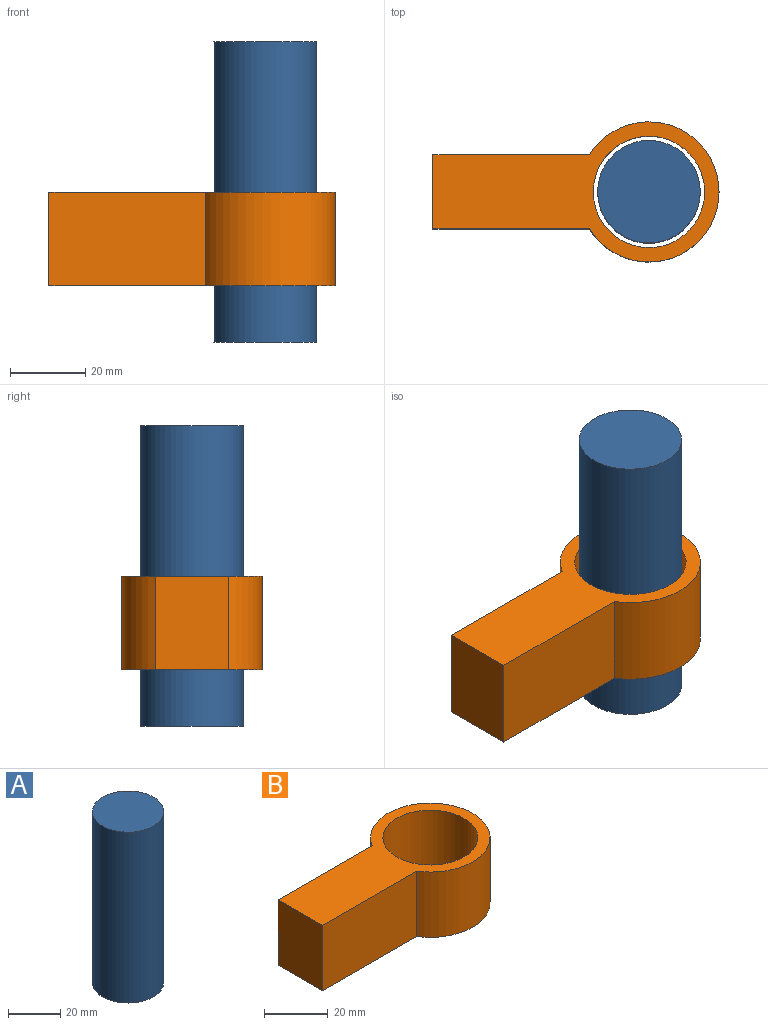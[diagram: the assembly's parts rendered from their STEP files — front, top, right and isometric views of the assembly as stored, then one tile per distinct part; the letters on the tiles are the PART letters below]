
ASSEMBLY  parts=2 mates=1
PART A: 3 faces, bbox 27.3x27.3x80 mm
  f0: cylinder r=13.66mm len=80mm, axis (0,0,-1), area 6865.6mm2, adj f1,f2
  f1: plane 27.32x27.32mm, normal (0,0,1), area 586.1mm2, adj f0
  f2: plane 27.32x27.32mm, normal (0,0,-1), area 586.1mm2, adj f0
PART B: 7 faces, bbox 76.2x37.3x25 mm
  f0: cylinder r=18.67mm len=37.34mm, axis (0,0,-1), area 2414.9mm2, adj f1,f4,f5,f6
  f1: plane 41.66x25mm, normal (0,1,0), area 1041.6mm2, adj f0,f2,f5,f6
  f2: plane 25x19.68mm, normal (-1,0,0), area 491.9mm2, adj f1,f4,f5,f6
  f3: cylinder r=14.84mm len=29.68mm, axis (0,0,-1), area 2331.4mm2, adj f5,f6
  f4: plane 41.66x25mm, normal (0,-1,0), area 1041.6mm2, adj f0,f2,f5,f6
  f5: plane 76.21x37.34mm, normal (0,0,1), area 1185.7mm2, adj f0,f1,f2,f3,f4
  f6: plane 76.21x37.34mm, normal (0,0,-1), area 1185.7mm2, adj f0,f1,f2,f3,f4
PLACE A t=(-34.48,16.75,-12.55)mm
PLACE B t=(-34.48,16.75,-78.55)mm
MATE revolute B.f3 <-> A.f0  axis (0,0,1) through (-34.48,16.75,27.45)mm
